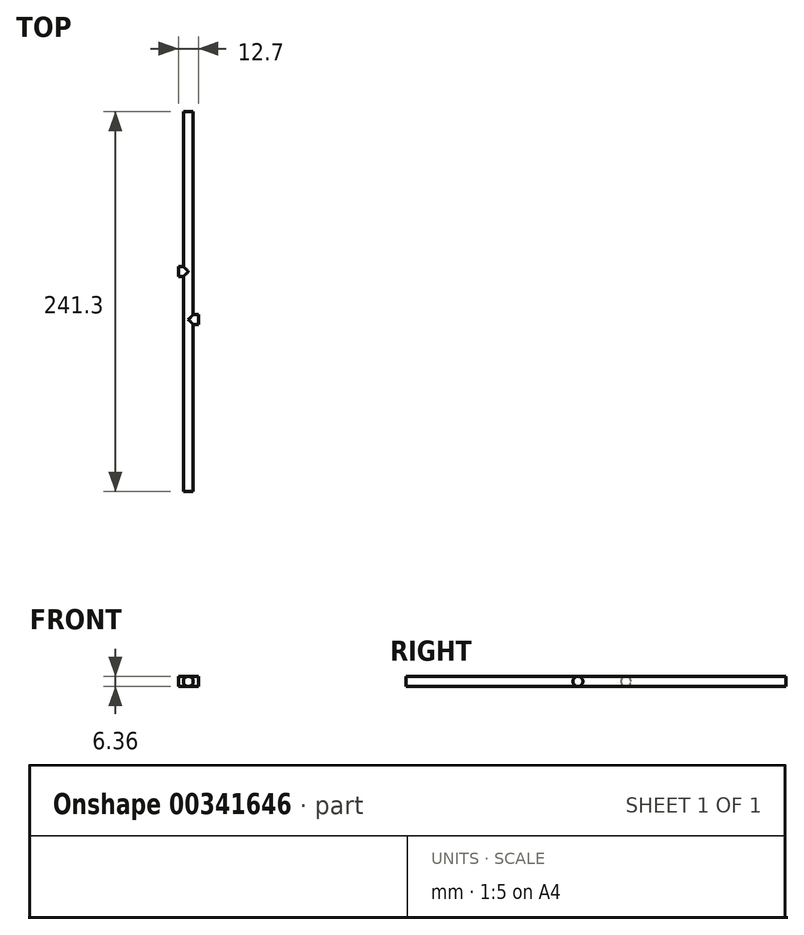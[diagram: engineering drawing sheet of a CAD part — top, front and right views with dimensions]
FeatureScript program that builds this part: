
annotation { "Feature Type Name" : "Feature", "Feature Type Description" : "" }
export const myFeature = defineFeature(function(context is Context, id is Id, definition is map)
    precondition{}
    {
        {
            var Q0;
            Q0=qCreatedBy(makeId("Front.planeOp"),FACE);
            var sketch = newSketch(context, id + "F0", { "sketchPlane" : qUnion([Q0])});
            skCircle(sketch, "E0", {"center": v(0, 0) * mm, "radius": 3.18 * mm});
            skSolve(sketch);
        }
        {
            var Q0;
            Q0=makeQuery(id+"F0.imprint","IMPRINT",FACE,{"disambiguationData":[TD([[makeQuery(id+"F0.imprint","IMPRINT",EDGE,{"derivedFrom":sQuery(id+"F0.wireOp",EDGE,"E0")}),1.0]])]});
            extrude(context, id + "F1", {"entities" : qUnion([Q0]), "oppositeDirection" : true, "depth" : 241.3 * mm});
        }
        {
            var Q0;
            Q0=qCreatedBy(makeId("Top.planeOp"),FACE);
            var sketch = newSketch(context, id + "F2", { "sketchPlane" : qUnion([Q0])});
            skLineSegment(sketch, "E1", {"start": v(-3.18, 0) * mm, "end": v(-3.18, 241.3) * mm});
            skLineSegment(sketch, "E2", {"start": v(3.18, 241.3) * mm, "end": v(3.18, 0) * mm});
            skSolve(sketch);
        }
        {
            var Q0;
            Q0=qCreatedBy(makeId("Right.planeOp"),FACE);
            var sketch = newSketch(context, id + "F3", { "sketchPlane" : qUnion([Q0])});
            skLineSegment(sketch, "E3.0", {"start": v(241.3, 0) * mm, "end": v(0, 0) * mm});
            skCircle(sketch, "E4", {"center": v(109.22, 0) * mm, "radius": 3.18 * mm});
            skSolve(sketch);
        }
        {
            var Q0;
            Q0 = qSketchRegion(id + "F3", true);
            extrude(context, id + "F4", {"entities" : qUnion([Q0]), "operationType" : NewBodyOperationType.ADD, "depth" : 6.35 * mm});
        }
        {
            var Q0;
            Q0=qCreatedBy(makeId("Right.planeOp"),FACE);
            var sketch = newSketch(context, id + "F5", { "sketchPlane" : qUnion([Q0])});
            skLineSegment(sketch, "E5.0", {"start": v(241.3, 0) * mm, "end": v(0, 0) * mm});
            skCircle(sketch, "E6", {"center": v(139.7, 0) * mm, "radius": 3.18 * mm});
            skSolve(sketch);
        }
        {
            var Q0;
            Q0 = qSketchRegion(id + "F5", true);
            extrude(context, id + "F6", {"entities" : qUnion([Q0]), "operationType" : NewBodyOperationType.ADD, "oppositeDirection" : true, "depth" : 6.35 * mm});
        }
    });
